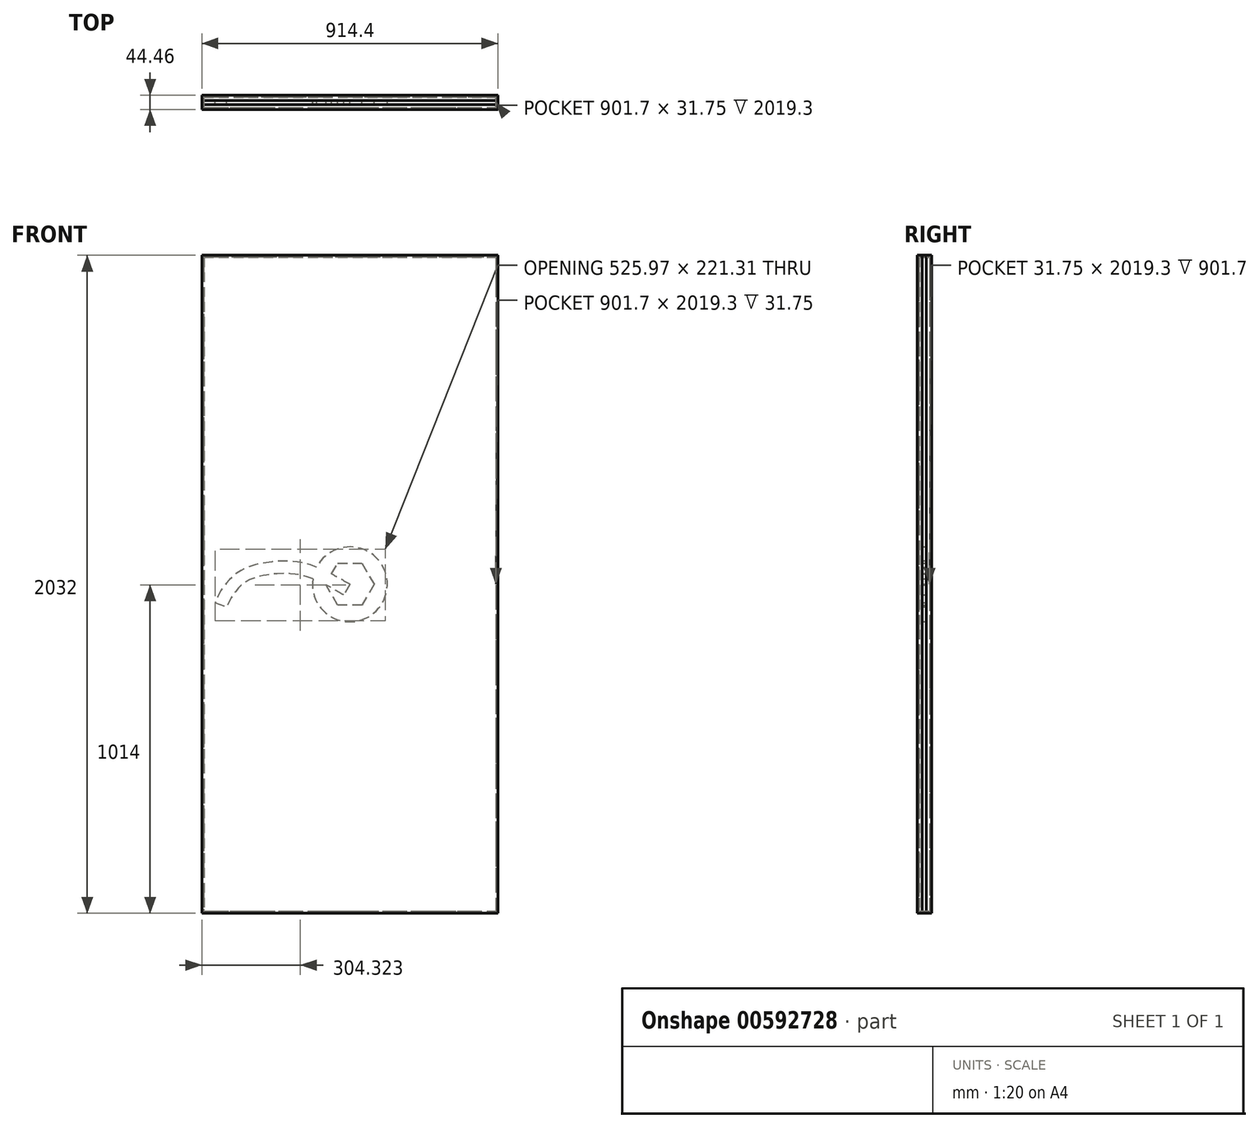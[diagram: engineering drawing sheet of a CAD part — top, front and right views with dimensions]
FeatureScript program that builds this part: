
annotation { "Feature Type Name" : "Feature", "Feature Type Description" : "" }
export const myFeature = defineFeature(function(context is Context, id is Id, definition is map)
    precondition{}
    {
        {
            var Q0;
            Q0=qCreatedBy(makeId("Front.planeOp"),FACE);
            var sketch = newSketch(context, id + "F0", { "sketchPlane" : qUnion([Q0])});
            skLineSegment(sketch, "E0.bottom", {"start": v(-457.2, 1016) * mm, "end": v(457.2, 1016) * mm});
            skLineSegment(sketch, "E0.top", {"start": v(-457.2, -1016) * mm, "end": v(457.2, -1016) * mm});
            skLineSegment(sketch, "E0.left", {"start": v(-457.2, 1016) * mm, "end": v(-457.2, -1016) * mm});
            skLineSegment(sketch, "E0.right", {"start": v(457.2, 1016) * mm, "end": v(457.2, -1016) * mm});
            skPoint(sketch, "E0.middle", {"position": v(0, 0) * mm});
            skSolve(sketch);
        }
        {
            var Q0;
            Q0 = qSketchRegion(id + "F0", true);
            extrude(context, id + "F1", {"entities" : qUnion([Q0]), "endBound" : BoundingType.SYMMETRIC, "depth" : 44.45 * mm, "offsetDistance" : 25.4 * mm});
        }
        {
            var Q0;
            Q0=makeQuery(id+"F1.opExtrude","CAP_FACE",FACE,{"disambiguationData":[OSD([sQuery(id+"F0.wireOp",EDGE,"E0.bottom"),sQuery(id+"F0.wireOp",EDGE,"E0.top"),sQuery(id+"F0.wireOp",EDGE,"E0.left"),sQuery(id+"F0.wireOp",EDGE,"E0.right")])],"isStart":false});
            var Q1;
            Q1=makeQuery(id+"F1.opExtrude","SWEPT_BODY",BODY,{"disambiguationData":[OSD([sQuery(id+"F0.wireOp",EDGE,"E0.bottom"),sQuery(id+"F0.wireOp",EDGE,"E0.top"),sQuery(id+"F0.wireOp",EDGE,"E0.left"),sQuery(id+"F0.wireOp",EDGE,"E0.right")])]});
            shell(context, id + "F2", {"isHollow" : true, "entities" : qUnion([Q0]), "parts" : qUnion([Q1]), "thickness" : 6.35 * mm});
        }
        {
            var Q0;
            Q0=qCreatedBy(makeId("Front.planeOp"),FACE);
            var sketch = newSketch(context, id + "F3", { "sketchPlane" : qUnion([Q0])});
            skCircle(sketch, "E1.cCircle", {"center": v(0, 0) * mm, "radius": 64.65 * mm, "construction": true});
            skLineSegment(sketch, "E1.0", {"start": v(-37.33, 64.65) * mm, "end": v(37.33, 64.65) * mm});
            skLineSegment(sketch, "E1.1", {"start": v(37.33, 64.65) * mm, "end": v(74.66, 0) * mm});
            skLineSegment(sketch, "E1.2", {"start": v(74.66, 0) * mm, "end": v(37.33, -64.65) * mm});
            skLineSegment(sketch, "E1.3", {"start": v(37.33, -64.65) * mm, "end": v(-37.33, -64.65) * mm});
            skLineSegment(sketch, "E1.4", {"start": v(-37.33, -64.65) * mm, "end": v(-74.66, 0) * mm});
            skLineSegment(sketch, "E1.5", {"start": v(-74.66, 0) * mm, "end": v(-37.33, 64.65) * mm});
            skPoint(sketch, "E1.0.midPoint", {"position": v(0, 64.65) * mm});
            skCircle(sketch, "E2", {"center": v(0, 0) * mm, "radius": 74.66 * mm});
            skCircle(sketch, "E3", {"center": v(0, 0) * mm, "radius": 115.67 * mm});
            skPoint(sketch, "E4.3.internal.snap0", {"position": v(-56, 32.33) * mm});
            skFitSpline(sketch, "E4", {"points": [v(0, 0) * mm, v(-140.2, 64.65) * mm, v(-272.93, 64.65) * mm, v(-352.05, 32.33) * mm, v(-400.55, -23.09) * mm, v(-415.86, -56.27) * mm], "startDerivative": vector(-526.9, 308.07) * mm, "endDerivative": vector(-93.81, -245.46) * mm});
            skFitSpline(sketch, "E5.0", {"points": [v(-19.23, -32.9) * mm, v(-30.2, -26.47) * mm, v(-46.4, -17) * mm, v(-67.58, -5.32) * mm, v(-83.25, 2.82) * mm, v(-98.74, 10.2) * mm, v(-114.03, 16.7) * mm, v(-126.63, 21.28) * mm, v(-135.38, 24) * mm, v(-140.36, 25.41) * mm, v(-144.08, 26.4) * mm, v(-147.18, 27.16) * mm, v(-149.66, 27.73) * mm, v(-153.39, 28.56) * mm, v(-159.04, 29.67) * mm, v(-166.67, 30.9) * mm, v(-174.4, 31.87) * mm, v(-182.18, 32.6) * mm, v(-192.6, 33.27) * mm, v(-205.68, 33.53) * mm, v(-221.25, 33.02) * mm, v(-233.97, 31.97) * mm, v(-243.9, 30.81) * mm, v(-251.2, 29.79) * mm, v(-257.16, 28.83) * mm, v(-261.82, 28) * mm, v(-265.26, 27.34) * mm, v(-268.64, 26.66) * mm, v(-273.04, 25.73) * mm, v(-278.34, 24.5) * mm, v(-284.38, 22.93) * mm, v(-292.04, 20.7) * mm, v(-300.9, 17.63) * mm, v(-308.89, 14.17) * mm, v(-314.86, 11.13) * mm, v(-319.16, 8.7) * mm, v(-323.3, 6.1) * mm, v(-326.31, 4) * mm, v(-328.29, 2.53) * mm, v(-329.6, 1.54) * mm, v(-331.24, 0.25) * mm, v(-333.22, -1.38) * mm, v(-335.86, -3.64) * mm, v(-339.15, -6.64) * mm, v(-343.03, -10.46) * mm, v(-346.82, -14.46) * mm, v(-350.47, -18.58) * mm, v(-353.97, -22.77) * mm, v(-357.27, -26.99) * mm, v(-360.36, -31.17) * mm, v(-363.2, -35.25) * mm, v(-365.33, -38.53) * mm, v(-366.9, -41.04) * mm, v(-367.98, -42.85) * mm, v(-369, -44.6) * mm, v(-370.27, -46.9) * mm, v(-371.72, -49.65) * mm, v(-373.29, -52.86) * mm, v(-375.22, -57.1) * mm, v(-377.47, -62.53) * mm, v(-379.3, -67.31) * mm, v(-380.27, -69.87) * mm]});
            skLineSegment(sketch, "E6.0", {"start": v(-457.2, 1016) * mm, "end": v(-457.2, -1016) * mm});
            skLineSegment(sketch, "E6.1", {"start": v(457.2, 1016) * mm, "end": v(-457.2, 1016) * mm});
            skLineSegment(sketch, "E6.2", {"start": v(457.2, -1016) * mm, "end": v(457.2, 1016) * mm});
            skLineSegment(sketch, "E6.3", {"start": v(-457.2, -1016) * mm, "end": v(457.2, -1016) * mm});
            skLineSegment(sketch, "E7", {"start": v(-415.86, -56.27) * mm, "end": v(-380.27, -69.87) * mm});
            skLineSegment(sketch, "E8", {"start": v(0, 0) * mm, "end": v(-19.23, -32.9) * mm});
            skFitSpline(sketch, "E9.0", {"points": [v(-6.41, -10.96) * mm, v(-17.39, -4.55) * mm, v(-33.76, 5.03) * mm, v(-55.55, 17.05) * mm, v(-71.89, 25.54) * mm, v(-88.26, 33.35) * mm, v(-104.67, 40.33) * mm, v(-118.42, 45.33) * mm, v(-129.47, 48.77) * mm, v(-137.8, 51.05) * mm, v(-146.14, 53.02) * mm, v(-154.58, 54.68) * mm, v(-163.07, 56.05) * mm, v(-174.47, 57.49) * mm, v(-188.76, 58.6) * mm, v(-205.86, 58.94) * mm, v(-222.72, 58.39) * mm, v(-239.18, 57.03) * mm, v(-252.44, 55.32) * mm, v(-262.68, 53.66) * mm, v(-268.9, 52.51) * mm, v(-273.78, 51.54) * mm, v(-278.56, 50.52) * mm, v(-284.38, 49.17) * mm, v(-291.12, 47.42) * mm, v(-299.78, 44.9) * mm, v(-310.04, 41.35) * mm, v(-319.6, 37.22) * mm, v(-326.88, 33.51) * mm, v(-332.17, 30.52) * mm, v(-337.3, 27.3) * mm, v(-341.47, 24.4) * mm, v(-344.74, 21.95) * mm, v(-347.97, 19.4) * mm, v(-351.96, 16.05) * mm, v(-356.64, 11.78) * mm, v(-362.68, 5.83) * mm, v(-369.84, -1.99) * mm, v(-376.31, -10) * mm, v(-381, -16.37) * mm, v(-384.26, -21.05) * mm, v(-386.74, -24.85) * mm, v(-388.57, -27.8) * mm, v(-390.3, -30.68) * mm, v(-392.27, -34.15) * mm, v(-395.07, -39.48) * mm, v(-398.05, -45.83) * mm, v(-401.11, -53.24) * mm, v(-403.02, -58.25) * mm, v(-404, -60.8) * mm]});
            skLineSegment(sketch, "E9.1", {"start": v(-17.38, -4.56) * mm, "end": v(-23.79, -15.52) * mm});
            skFitSpline(sketch, "E9.2", {"points": [v(-12.82, -21.93) * mm, v(-23.8, -15.5) * mm, v(-40.09, -5.99) * mm, v(-61.56, 5.86) * mm, v(-77.57, 14.18) * mm, v(-93.5, 21.78) * mm, v(-109.35, 28.51) * mm, v(-122.53, 33.3) * mm, v(-133.05, 36.58) * mm, v(-139.62, 38.38) * mm, v(-144.88, 39.68) * mm, v(-150.15, 40.87) * mm, v(-156.8, 42.18) * mm, v(-164.87, 43.47) * mm, v(-173, 44.5) * mm, v(-181.18, 45.27) * mm, v(-192.1, 45.97) * mm, v(-205.77, 46.24) * mm, v(-221.98, 45.7) * mm, v(-235.2, 44.61) * mm, v(-245.52, 43.4) * mm, v(-253.1, 42.35) * mm, v(-259.28, 41.35) * mm, v(-264.12, 40.48) * mm, v(-267.7, 39.8) * mm, v(-271.21, 39.1) * mm, v(-275.8, 38.12) * mm, v(-281.36, 36.84) * mm, v(-287.75, 35.18) * mm, v(-295.91, 32.8) * mm, v(-305.46, 29.5) * mm, v(-314.24, 25.7) * mm, v(-320.87, 22.32) * mm, v(-325.66, 19.6) * mm, v(-330.3, 16.7) * mm, v(-334.06, 14.08) * mm, v(-337, 11.88) * mm, v(-339.94, 9.57) * mm, v(-343.58, 6.5) * mm, v(-347.9, 2.57) * mm, v(-352.1, -1.57) * mm, v(-356.18, -5.88) * mm, v(-361.41, -11.77) * mm, v(-366.28, -17.8) * mm, v(-370.68, -23.77) * mm, v(-373.73, -28.15) * mm, v(-376.04, -31.7) * mm, v(-377.73, -34.42) * mm, v(-379.32, -37.07) * mm, v(-381.12, -40.25) * mm, v(-383.04, -43.9) * mm, v(-384.78, -47.44) * mm, v(-386.36, -50.92) * mm, v(-387.85, -54.4) * mm, v(-389.28, -57.93) * mm, v(-390.7, -61.56) * mm, v(-391.65, -64.06) * mm, v(-392.14, -65.34) * mm]});
            skLineSegment(sketch, "E9.3", {"start": v(-399.34, -48.99) * mm, "end": v(-387.47, -53.52) * mm});
            skCircle(sketch, "E10", {"center": v(-91.57, 28.03) * mm, "radius": 7.14 * mm});
            skSolve(sketch);
        }
        {
            var Q0;
            Q0 = qSketchRegion(id + "F3", true);
            var Q1;
            Q1=makeQuery(id+"F3.imprint","IMPRINT",FACE,{"disambiguationData":[TD([[makeQuery(id+"F3.imprint","IMPRINT",EDGE,{"derivedFrom":sQuery(id+"F3.wireOp",EDGE,"ZeUrsKBT-qRSO-O101-3QiZ-ebdeJ3SFFelu")}),-1.0]])]});
            var Q2;
            {var subQ6=sQuery(id+"F3.wireOp",EDGE,"6vdhy7az-vN8k-Mucr-5gng-MiiJ38igQo3p");var subQ11=makeQuery(id+"F3.imprint","INTERSECT",VERTEX,{"derivedFrom":[subQ6,sQuery(id+"F3.wireOp",EDGE,"12e6a44a-b526-4e30-bfd3-669c1ef6b0c8.1.0")]});Q2=makeQuery(id+"F3.imprint","IMPRINT",FACE,{"disambiguationData":[TD([[makeQuery(id+"F3.imprint","IMPRINT",EDGE,{"disambiguationData":[TD([[subQ11,1.0]])],"derivedFrom":subQ6}),1.0]])]});}
            var Q3;
            Q3=makeQuery(id+"F3.imprint","IMPRINT",FACE,{"disambiguationData":[TD([[makeQuery(id+"F3.imprint","IMPRINT",EDGE,{"derivedFrom":sQuery(id+"F3.wireOp",EDGE,"dVGxO5Qh-1T28-DAAB-Pbn9-705rf7LkHJGE")}),-1.0]])]});
            var Q4;
            Q4=makeQuery(id+"F3.imprint","IMPRINT",FACE,{"disambiguationData":[TD([[makeQuery(id+"F3.imprint","IMPRINT",EDGE,{"derivedFrom":sQuery(id+"F3.wireOp",EDGE,"knRrB5qz-hKjb-DpLd-SCs5-E6yy4BbjU2i2")}),-1.0]])]});
            var Q5;
            Q5=makeQuery(id+"F3.imprint","IMPRINT",FACE,{"disambiguationData":[TD([[makeQuery(id+"F3.imprint","IMPRINT",EDGE,{"derivedFrom":sQuery(id+"F3.wireOp",EDGE,"E1.0")}),-1.0]])]});
            extrude(context, id + "F4", {"entities" : qUnion([Q0, Q1, Q2, Q3, Q4, Q5]), "endBound" : BoundingType.SYMMETRIC, "depth" : 12.7 * mm, "offsetDistance" : 25.4 * mm});
        }
    });
